# Revit family: QF-Water_Processor-OptiPure-BWS350
name_source: partatom
category: Specialty Equipment
revit_build: Autodesk Revit 2017 (Build: 20160225_1515(x64)
units: mm (PartAtom-declared; Revit-internal decimal feet)

## family parameters
Always vertical = Yes
Cut with Voids When Loaded = No
OmniClass Number = 23.40.40.14
OmniClass Title = Food Service Equipment
Part Type = Normal
Room Calculation Point = No
Round Connector Dimension = Use Diameter
Shared = No
Work Plane-Based = No

## types (2) — shared parameters
Assembly Code = E1090300
Body Material = Mounting
Clearance Material = Clearance
Cold Water Maximum Pressure = 80.00 psi
Cold Water Minimum Pressure = 50.00 psi
Cold Water Size = 0"
Description = WATER FILTRATION SYSTEM
Feed Temperature Range = 40-100°F
Filtered Water Flow = 0 GPM
Filtered Water to Equipment = 1"
Filtered Water to Tank = 0"
Height = 26.7 "
Indirect Waste Flow = 2 GPM
Indirect Waste Size = 0"
Keynote = 11400
Length = 19.77 "
Manufacturer = OPTIPURE
Material = Plastic
Model = 164-14350 - BWS350 SYS
Tank Repressurization Return = 1"
Type Comments = REVERSE OSMOSIS, FOR COMBINATION APPLICATIONS
URL = WWW.OPTIPUREWATER.COM
Width = 8.44 "

## per-type parameters (varying)
| type | Cycle | Volts | Watts |
| BWS350 120VAC | 60 Hz | 120 V | 6 W |
| BWS350 230VAC | 50 Hz | 230 V | 0 W |

## geometry (parser evidence)
native form markers: Sweep x3
no freeform markers — native parametric forms only
